# Revit family: Louver-Channel_Frame-Carnes-Rectangular-Drainable_Blade_FVCB
name_source: partatom
category: Air Terminals
revit_build: Autodesk Revit MEP 2012 (Build: 20110916_2132(x64)
units: mm (PartAtom-declared; Revit-internal decimal feet)

## types (1)
- (See Type Catalog)
    04 CSI = 08 91 00
    95 CSI = 10200
    Airflow = 0 CFM
    Assembly Code = D3090700
    Blade Material = Steel - Carnes - Galvanized
    Catalog URL = http://www.carnes.com
    Connector Description 1 = Duct Connetor
    Default Elevation = 48"
    Description = Galvanized Steel Drainable Blade Louvers
    Frame Material = Steel - Carnes - Galvanized
    Free Area = 0 SF
    Free Area Note = See Spec Sheet URL
    Louver Height = 96"
    Louver Length = 6"
    Louver Width = 72"
    Manufacturer = Carnes Company
    Manufacturer Fax = 608-845-6470
    Maximum Horinzontal Size = 72"W x 96"H
    Maximum Size Note = Larger Sizes made in multiple sections
    Maximum Vertical Size = 72"W x 96"H
    Minimum Size = 8"W x 12"H
    Model = FVCB
    Outside Height = 97 1/2"
    Outside Width = 73 1/2"
    Pressure Drop = 0.00 Pa
    Product Line = Galvanized Steel Drainable Blade Louvers
    Product Page URL = http://www.carnes.com
    Specifications  URL = http://www.carnes.com
    Subcategory = Louvers and Dampers
    URL = http://www.carnes.com
    ecoScorecard Product Page = http://ecoscorecard.com

## geometry (parser evidence)
native form markers: Blend x4, Sweep x3
no freeform markers — native parametric forms only
